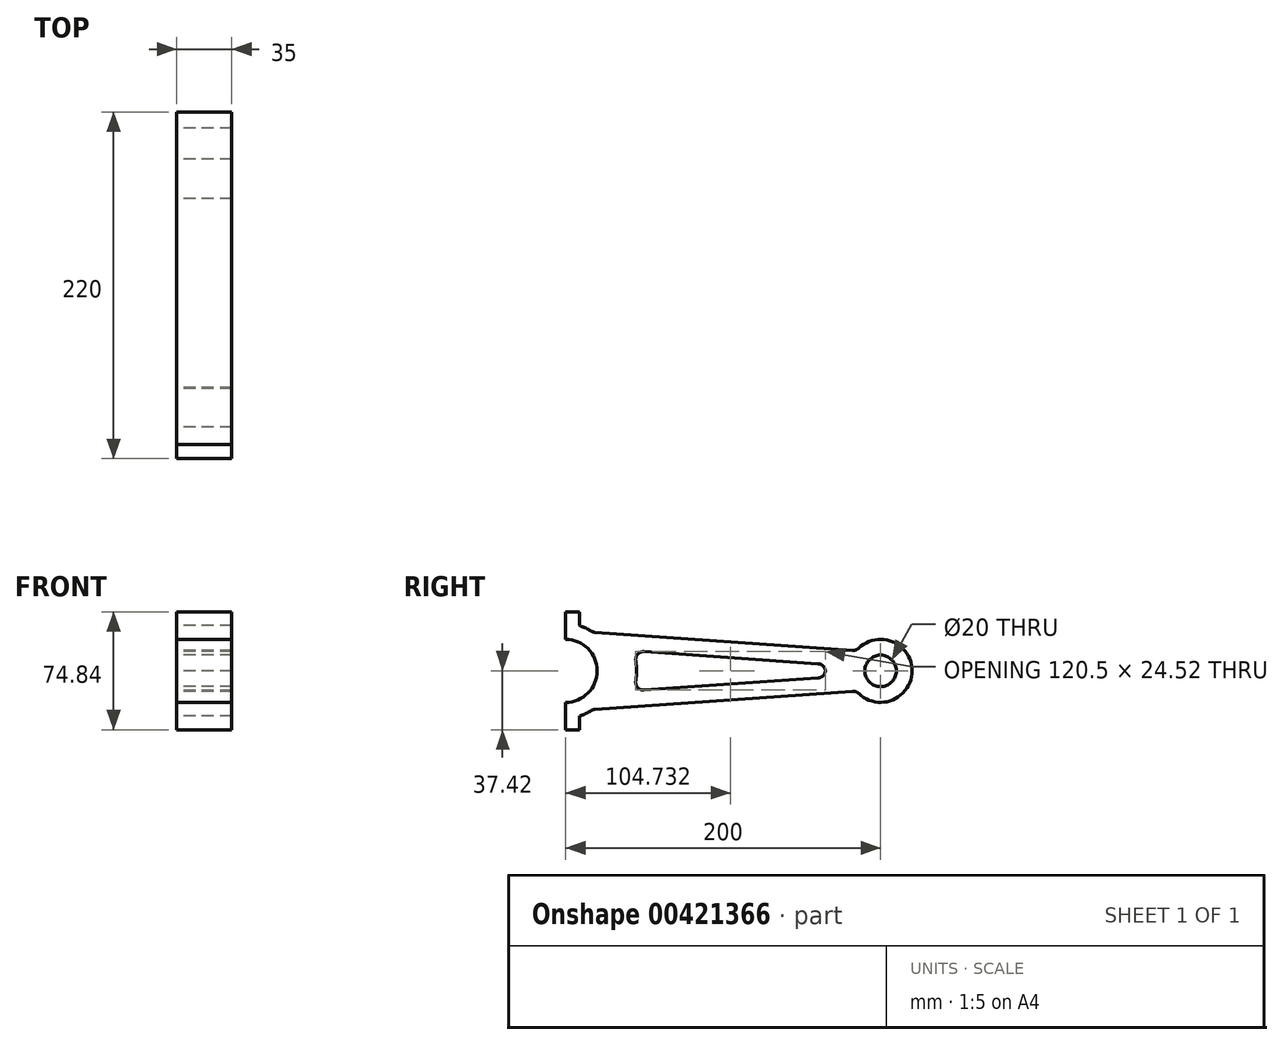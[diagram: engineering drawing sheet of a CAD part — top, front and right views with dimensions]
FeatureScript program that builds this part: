
annotation { "Feature Type Name" : "Feature", "Feature Type Description" : "" }
export const myFeature = defineFeature(function(context is Context, id is Id, definition is map)
    precondition{}
    {
        {
            var Q0;
            Q0=qCreatedBy(makeId("Right.planeOp"),FACE);
            var sketch = newSketch(context, id + "F0", { "sketchPlane" : qUnion([Q0])});
            skCircle(sketch, "E0", {"center": v(200, 0) * mm, "radius": 10 * mm});
            skArc(sketch, "E1", {"start": v(184.68, -12.86) * mm, "mid": v(220, 0) * mm, "end": v(184.68, 12.86) * mm});
            skArc(sketch, "E2", {"start": v(0, 20) * mm, "mid": v(20, 0) * mm, "end": v(0, -20) * mm});
            skLineSegment(sketch, "E3", {"start": v(0, 20) * mm, "end": v(0, 28.7) * mm});
            skLineSegment(sketch, "E4", {"start": v(0, 28.7) * mm, "end": v(8.7, 28.7) * mm, "construction": true});
            skLineSegment(sketch, "E5", {"start": v(0, -20) * mm, "end": v(0, -28.7) * mm});
            skLineSegment(sketch, "E6", {"start": v(0, -28.7) * mm, "end": v(8.7, -28.7) * mm, "construction": true});
            skArc(sketch, "E7", {"start": v(8.7, 28.7) * mm, "mid": v(13.13, 26.97) * mm, "end": v(17.22, 24.57) * mm});
            skLineSegment(sketch, "E8", {"start": v(184.68, -12.86) * mm, "end": v(17.22, -24.57) * mm});
            skLineSegment(sketch, "E9", {"start": v(184.68, 12.86) * mm, "end": v(17.22, 24.57) * mm});
            skArc(sketch, "E10", {"start": v(17.22, 24.57) * mm, "mid": v(30, 0) * mm, "end": v(17.22, -24.57) * mm, "construction": true});
            skArc(sketch, "E11", {"start": v(17.22, -24.57) * mm, "mid": v(13.13, -26.97) * mm, "end": v(8.7, -28.7) * mm});
            skLineSegment(sketch, "E12", {"start": v(0, 28.7) * mm, "end": v(0, 37.42) * mm});
            skLineSegment(sketch, "E13", {"start": v(0, 37.42) * mm, "end": v(8.7, 37.42) * mm});
            skLineSegment(sketch, "E14", {"start": v(8.7, 37.42) * mm, "end": v(8.7, 28.7) * mm});
            skLineSegment(sketch, "E15", {"start": v(0, -28.7) * mm, "end": v(0, -37.42) * mm});
            skLineSegment(sketch, "E16", {"start": v(0, -37.42) * mm, "end": v(8.7, -37.42) * mm});
            skLineSegment(sketch, "E17", {"start": v(8.7, -37.42) * mm, "end": v(8.7, -28.7) * mm});
            skArc(sketch, "E18", {"start": v(43.16, 12.73) * mm, "mid": v(45, 0) * mm, "end": v(43.16, -12.73) * mm});
            skLineSegment(sketch, "E19", {"start": v(43.16, 12.73) * mm, "end": v(165.25, 4.19) * mm});
            skLineSegment(sketch, "E20", {"start": v(43.16, -12.73) * mm, "end": v(165.25, -4.19) * mm});
            skArc(sketch, "E21", {"start": v(165.25, 4.19) * mm, "mid": v(165, 0) * mm, "end": v(165.25, -4.19) * mm});
            skLineSegment(sketch, "E22", {"start": v(184.68, 12.86) * mm, "end": v(200, 0) * mm, "construction": true});
            skLineSegment(sketch, "E23", {"start": v(184.68, -12.86) * mm, "end": v(200, 0) * mm, "construction": true});
            skSolve(sketch);
        }
        {
            var Q0;
            Q0=makeQuery(id+"F0.imprint","IMPRINT",FACE,{"disambiguationData":[TD([[makeQuery(id+"F0.imprint","IMPRINT",EDGE,{"derivedFrom":sQuery(id+"F0.wireOp",EDGE,"E0")}),-1.0]])]});
            extrude(context, id + "F1", {"entities" : qUnion([Q0]), "depth" : 35 * mm});
        }
        {
            var Q0;
            Q0=makeQuery(id+"F1.opExtrude","SWEPT_EDGE",EDGE,{"disambiguationData":[OSD([sQuery(id+"F0.wireOp",EDGE,"E7"),sQuery(id+"F0.wireOp",EDGE,"E9")])]});
            var Q1;
            Q1=makeQuery(id+"F1.opExtrude","SWEPT_EDGE",EDGE,{"disambiguationData":[OSD([sQuery(id+"F0.wireOp",EDGE,"E1"),sQuery(id+"F0.wireOp",EDGE,"E9")])]});
            var Q2;
            Q2=makeQuery(id+"F1.opExtrude","SWEPT_EDGE",EDGE,{"disambiguationData":[OSD([sQuery(id+"F0.wireOp",EDGE,"E1"),sQuery(id+"F0.wireOp",EDGE,"E8")])]});
            var Q3;
            Q3=makeQuery(id+"F1.opExtrude","SWEPT_EDGE",EDGE,{"disambiguationData":[OSD([sQuery(id+"F0.wireOp",EDGE,"E8"),sQuery(id+"F0.wireOp",EDGE,"E11")])]});
            var Q4;
            Q4=makeQuery(id+"F1.opExtrude","SWEPT_EDGE",EDGE,{"disambiguationData":[OSD([sQuery(id+"F0.wireOp",EDGE,"E19"),sQuery(id+"F0.wireOp",EDGE,"E21")])]});
            var Q5;
            Q5=makeQuery(id+"F1.opExtrude","SWEPT_EDGE",EDGE,{"disambiguationData":[OSD([sQuery(id+"F0.wireOp",EDGE,"E20"),sQuery(id+"F0.wireOp",EDGE,"E21")])]});
            var Q6;
            Q6=makeQuery(id+"F1.opExtrude","SWEPT_EDGE",EDGE,{"disambiguationData":[OSD([sQuery(id+"F0.wireOp",EDGE,"E18"),sQuery(id+"F0.wireOp",EDGE,"E19")])]});
            var Q7;
            Q7=makeQuery(id+"F1.opExtrude","SWEPT_EDGE",EDGE,{"disambiguationData":[OSD([sQuery(id+"F0.wireOp",EDGE,"E18"),sQuery(id+"F0.wireOp",EDGE,"E20")])]});
            fillet(context, id + "F2", {"entities" : qUnion([Q0, Q1, Q2, Q3, Q4, Q5, Q6, Q7]), "radius" : 5 * mm, "tangentPropagation" : true, "allowEdgeOverflow" : false});
        }
    });
